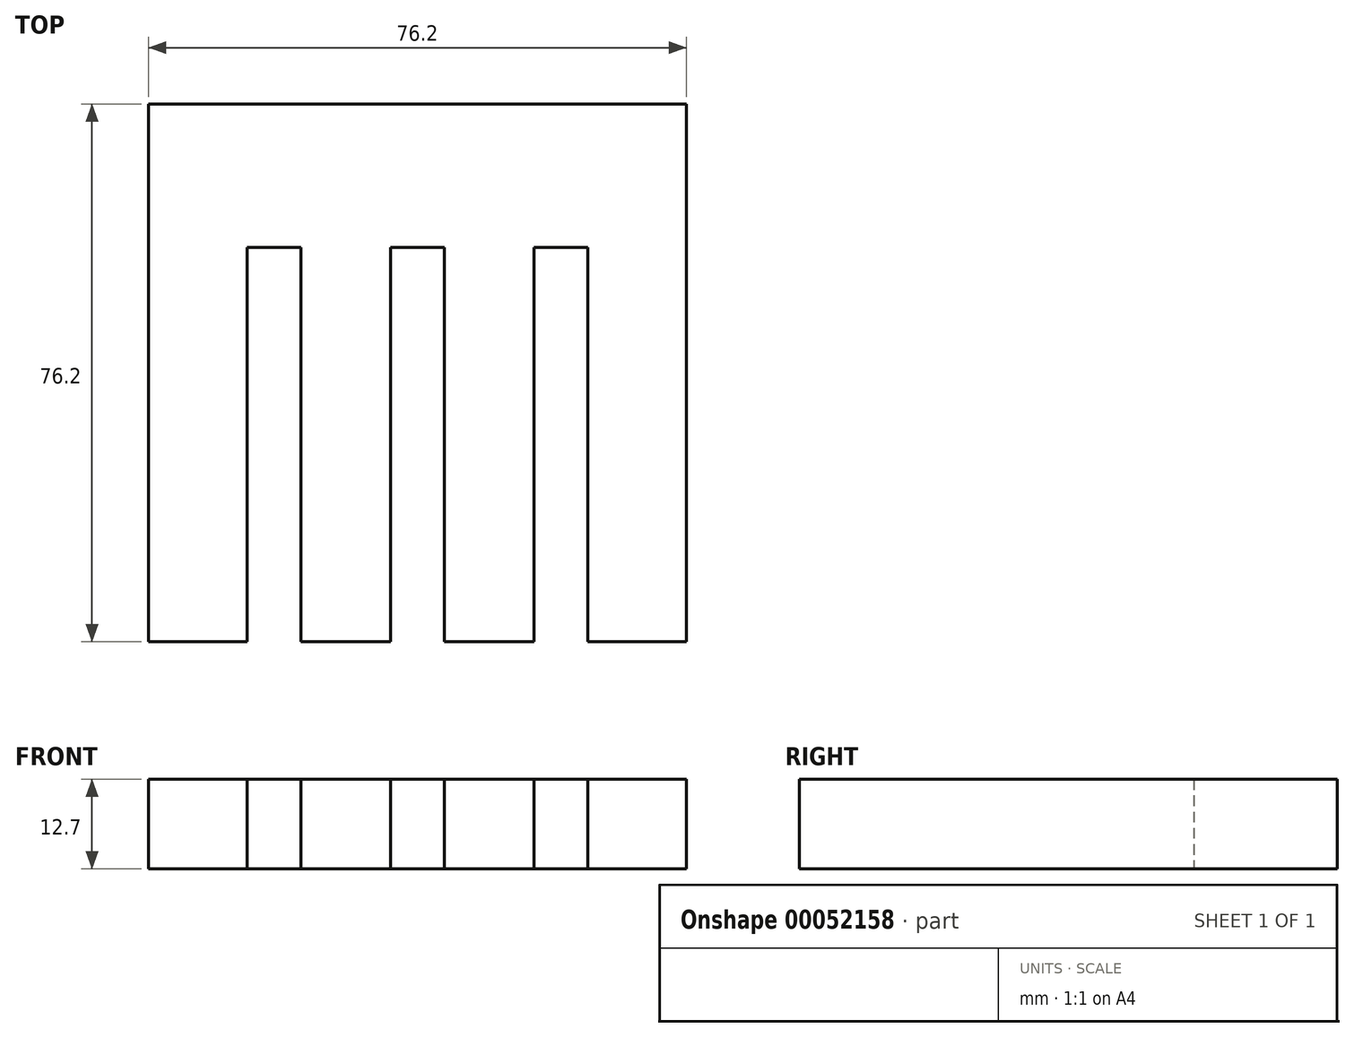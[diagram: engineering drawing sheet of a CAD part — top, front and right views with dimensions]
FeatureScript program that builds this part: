
annotation { "Feature Type Name" : "Feature", "Feature Type Description" : "" }
export const myFeature = defineFeature(function(context is Context, id is Id, definition is map)
    precondition{}
    {
        {
            var Q0;
            Q0=qCreatedBy(makeId("Top.planeOp"),FACE);
            var sketch = newSketch(context, id + "F0", { "sketchPlane" : qUnion([Q0])});
            skLineSegment(sketch, "E0.rect.bottom", {"start": v(38.1, 38.1) * mm, "end": v(-38.1, 38.1) * mm});
            skLineSegment(sketch, "E0.rect.top", {"start": v(38.1, -38.1) * mm, "end": v(24.13, -38.1) * mm});
            skLineSegment(sketch, "E0.rect.left", {"start": v(38.1, 38.1) * mm, "end": v(38.1, -38.1) * mm});
            skLineSegment(sketch, "E0.rect.right", {"start": v(-38.1, 38.1) * mm, "end": v(-38.1, -38.1) * mm});
            skPoint(sketch, "E0.rect.middle", {"position": v(0, 0) * mm});
            skLineSegment(sketch, "E1", {"start": v(-24.13, -38.1) * mm, "end": v(-24.13, 17.78) * mm});
            skLineSegment(sketch, "E2", {"start": v(-24.13, 17.78) * mm, "end": v(-16.51, 17.78) * mm});
            skLineSegment(sketch, "E3", {"start": v(-16.51, 17.78) * mm, "end": v(-16.51, -38.1) * mm});
            skLineSegment(sketch, "E4", {"start": v(-3.8, -38.1) * mm, "end": v(-3.81, 17.78) * mm});
            skLineSegment(sketch, "E5", {"start": v(-3.81, 17.78) * mm, "end": v(3.8, 17.78) * mm});
            skLineSegment(sketch, "E6", {"start": v(3.8, 17.78) * mm, "end": v(3.8, -38.1) * mm});
            skLineSegment(sketch, "E7", {"start": v(16.5, -38.1) * mm, "end": v(16.5, 17.78) * mm});
            skLineSegment(sketch, "E8", {"start": v(16.5, 17.78) * mm, "end": v(24.13, 17.78) * mm});
            skLineSegment(sketch, "E9", {"start": v(24.13, 17.78) * mm, "end": v(24.13, -38.1) * mm});
            skLineSegment(sketch, "E10.trimOffspring", {"start": v(-24.13, -38.1) * mm, "end": v(-38.1, -38.1) * mm});
            skLineSegment(sketch, "E11.trimOffspring", {"start": v(-3.81, -38.1) * mm, "end": v(-16.51, -38.1) * mm});
            skLineSegment(sketch, "E12.trimOffspring", {"start": v(16.5, -38.1) * mm, "end": v(3.8, -38.1) * mm});
            skSolve(sketch);
        }
        {
            var Q0;
            Q0=makeQuery(id+"F0.imprint","IMPRINT",FACE,{"disambiguationData":[TD([[makeQuery(id+"F0.imprint","IMPRINT",EDGE,{"derivedFrom":sQuery(id+"F0.wireOp",EDGE,"E0.rect.bottom")}),1.0]])]});
            extrude(context, id + "F1", {"entities" : qUnion([Q0]), "depth" : 12.7 * mm});
        }
    });
